# Revit family: LWplc_Latchwaysplc_FallArrestSystemGuidedAnchorLine_StandingSeamType
name_source: partatom
category: Generic Models
revit_build: Autodesk Revit 2014 (Build: 20130709_2115(x64)
units: mm (PartAtom-declared; Revit-internal decimal feet)

## types (7) — shared parameters
AssetType = Fixed
AttachmentDeviceGuide = www.latchways.com/BIM/Latchways_Attachment_Device_Guide.pdf
BaseCorner = 10 mm  [stored 0.0328084 ft]
Color = Dome: Stainless Steel, Electro Polished
Description = Latchways ManSafe® for Standing Seam Roofing, using Constant Force posts
DurationUnit = year
FireExit = No
FixingDetail = www.latchways.com/BIM/Latchways_CFP_StandingSeam_FixingDetail.pdf
FixingHole = 7 mm  [stored 0.0229659 ft]
Height = 193 mm
IfcExportAs = NOTDEFINED
IfcExportType = IfcTransportElement
ManSafeForRoofingBrochure = www.latchways.com/BIM/MansafeForRoofing.pdf
ManufacturerName = Latchways plc
ManufacturerURL = www.latchways.com
Material = Dome: 316s Stainless Steel; Base Plate: Aluminium, Powder Coat
NBSDescription = Fall arrest system - guided anchor line
NBSReference = 80-50-25/110
PreInstallationSurvey = Required
ProductSpecification = www.latchways.com/BIM/Latchways_CFP_StandingSeam_NBS_Specifications.doc
SlotArray1X = 26 mm
SlotArray1Y = 13 mm
SystemMaintenance = Annual service to be completed by registered Latchways installer in accordance with BS7883:2005
SystemManufacturer = Latchways plc
URL = www.latchways.com
Uniclass2 = 80-30-25/135
Version = 1
WarrantyDurationUnit = year

## per-type parameters (varying)
| type | BIMObjectName | BasePlateLength | BasePlateWidth | BaseThickness | BlendBaseL | BlendBaseRad | BlendBaseW | Model | ModelNumber | ModelReference | Name | NominalHeight | NominalLength | NominalWidth | ProductInformation | Size | Slot1Offset | SlotArray1 | SlotArray2 | SlotArray2X | SlotArray2Y | SlotArray3 | SlotArray4 |
| CFP Standing Seam Tapered 295 mm to 525 mm | LWplc_Latchwaysplc_FallArrestSystemGuidedAnchorLine_StandingSeamType_Tapered295to525mm | 280 mm  [stored 0.918635 ft] | 198 mm  [stored 0.649606 ft] | 3 mm  [stored 0.00984252 ft] | 85 mm  [stored 0.278871 ft] | 20 mm  [stored 0.0656168 ft] | 50 mm  [stored 0.164042 ft] | 65664-00 | 65664-00 | Constant Force Post Standing Seam Roofing (Tapered) 295 mm to 525 mm | FallArrestSystemGuidedAnchorLine_StandingSeamType_Tapered295to525mm_Latchwaysplc | 195 mm  [stored 0.639764 ft] | 560 mm | 396 mm  [stored 1.29921 ft] | www.latchways.com/BIM/65664-00_LatchwaysConstantForcePost_StandingSeam_Tapered_295-525.pdf | 560 x 396 x 195 mm | 0 mm  [stored 0 ft] | No | Yes | 62 mm | 17 mm | No | No |
| CFP Standing Seam for Butler 600 mm MR24 | LWplc_Latchwaysplc_FallArrestSystemGuidedAnchorLine_StandingSeamType_Butler600mmMR24 | 330 mm | 200 mm  [stored 0.656168 ft] | 13 mm | 55 mm  [stored 0.180446 ft] | 10 mm  [stored 0.0328084 ft] | 25 mm  [stored 0.082021 ft] | 65618-00 | 65618-00 | Constant Force Post Standing Seam Roofing For Butler 600 mm MR24 | FallArrestSystemGuidedAnchorLine_StandingSeamType_Butler600mmMR24_Latchwaysplc | 206 mm | 660 mm | 400 mm  [stored 1.31234 ft] | www.latchways.com/BIM/65618-00_LatchwaysConstantForcePost_StandingSeam_600_MR24.pdf | 660 x 400 x 205.5 mm | 0 mm  [stored 0 ft] | No | No | 62 mm | 17 mm | Yes | No |
| CFP Standing Seam 300 or 305 mm x 400 mm seam pitch | LWplc_Latchwaysplc_FallArrestSystemGuidedAnchorLine_StandingSeamType_300or305mmx400mmSeamPitch | 230 mm  [stored 0.754593 ft] | 183 mm | 3 mm  [stored 0.00984252 ft] | 73 mm  [stored 0.239501 ft] | 20 mm  [stored 0.0656168 ft] | 36 mm  [stored 0.11811 ft] | 51001-00 | 51001-00 | Constant Force Post Standing Seam Roofing 300 or 305 mm x 400 mm Seam Pitch | FallArrestSystemGuidedAnchorLine_StandingSeamType_300or305mmx400mmSeamPitch_Latchwaysplc | 195 mm  [stored 0.639764 ft] | 460 mm | 365 mm  [stored 1.19751 ft] | www.latchways.com/BIM/51001-00_LatchwaysConstantForcePost_StandingSeam_300-305x400.pdf | 460 x 365 x 195 mm | 0 mm  [stored 0 ft] | Yes | No | 69 mm | 31 mm | No | No |
| CFP Standing Seam 333 mm and 500 mm seam pitch | LWplc_Latchwaysplc_FallArrestSystemGuidedAnchorLine_StandingSeamType_333x500mmSeamPitch | 280 mm  [stored 0.918635 ft] | 195 mm  [stored 0.639764 ft] | 3 mm  [stored 0.00984252 ft] | 82 mm  [stored 0.269029 ft] | 20 mm  [stored 0.0656168 ft] | 48 mm  [stored 0.15748 ft] | 51101-00 | 51101-00 | Constant Force Post Standing Seam Roofing 333 mm and 500 mm seam pitch | FallArrestSystemGuidedAnchorLine_StandingSeamType_333x500mmSeamPitch_Latchwaysplc | 195 mm  [stored 0.639764 ft] | 560 mm | 390 mm  [stored 1.27953 ft] | www.latchways.com/BIM/51101-00_LatchwaysConstantForcePost_StandingSeam_333x500.pdf | 560 x 390 x 195 mm | 0 mm  [stored 0 ft] | Yes | No | 62 mm | 17 mm | No | No |
| CFP Standing Seam 333 mm and 429 mm seam pitch | LWplc_Latchwaysplc_FallArrestSystemGuidedAnchorLine_StandingSeamType_333x429mmSeamPitch | 245 mm | 179 mm  [stored 0.58727 ft] | 3 mm  [stored 0.00984252 ft] | 49 mm  [stored 0.160761 ft] | 20 mm  [stored 0.0656168 ft] | 49 mm  [stored 0.160761 ft] | 51110-00 | 51110-00 | Constant Force Post Standing Seam Roofing 333 mm and 429 mm seam pitch | FallArrestSystemGuidedAnchorLine_StandingSeamType_333x429mmSeamPitch_Latchwaysplc | 195 mm  [stored 0.639764 ft] | 489 mm | 358 mm  [stored 1.17454 ft] | www.latchways.com/BIM/51110-00_LatchwaysConstantForcePost_StandingSeam_333x429.pdf | 489 x 358 x 195 mm | 0 mm  [stored 0 ft] | Yes | No | 62 mm | 17 mm | No | No |
| CFP Standing Seam 434 mm seam pitch | LWplc_Latchwaysplc_FallArrestSystemGuidedAnchorLine_StandingSeamType_434mmSeamPitch | 280 mm  [stored 0.918635 ft] | 198 mm  [stored 0.649606 ft] | 3 mm  [stored 0.00984252 ft] | 83 mm  [stored 0.27231 ft] | 20 mm  [stored 0.0656168 ft] | 48 mm  [stored 0.15748 ft] | 65613-00 | 65613-00 | Constant Force Post Standing Seam Roofing 434 mm Seam Pitch | FallArrestSystemGuidedAnchorLine_StandingSeamType_434mmSeamPitch_Latchwaysplc | 195 mm  [stored 0.639764 ft] | 560 mm | 396 mm  [stored 1.29921 ft] | www.latchways.com/BIM/65613-00_LatchwaysConstantForcePost_StandingSeam_434.pdf | 560 x 396 x 195 mm | 5 mm  [stored 0.0164042 ft] | No | No | 62 mm | 17 mm | No | Yes |
| CFP Standing Seam Tapered 380 mm to 610 mm | LWplc_Latchwaysplc_FallArrestSystemGuidedAnchorLine_StandingSeamType_Tapered380to610mm | 321 mm | 198 mm  [stored 0.649606 ft] | 3 mm  [stored 0.00984252 ft] | 125 mm  [stored 0.410105 ft] | 20 mm  [stored 0.0656168 ft] | 50 mm  [stored 0.164042 ft] | 65682-00 | 65682-00 | Constant Force Post Standing Seam Roofing (Tapered) 380 mm to 610 mm | FallArrestSystemGuidedAnchorLine_StandingSeamType_Tapered380to610mm_Latchwaysplc | 195 mm  [stored 0.639764 ft] | 643 mm | 396 mm  [stored 1.29921 ft] | www.latchways.com/BIM/65682-00_LatchwaysConstantForcePost_StandingSeam_Tapered_380-610.pdf | 643 x 396 x 195 mm | 0 mm  [stored 0 ft] | No | Yes | 62 mm | 17 mm | No | No |

note: [stored X ft] marks values corroborated as IEEE doubles in the binary element streams (Revit-internal decimal feet)

## geometry (parser evidence)
native form markers: Blend x3, Sweep x13
no freeform markers — native parametric forms only
